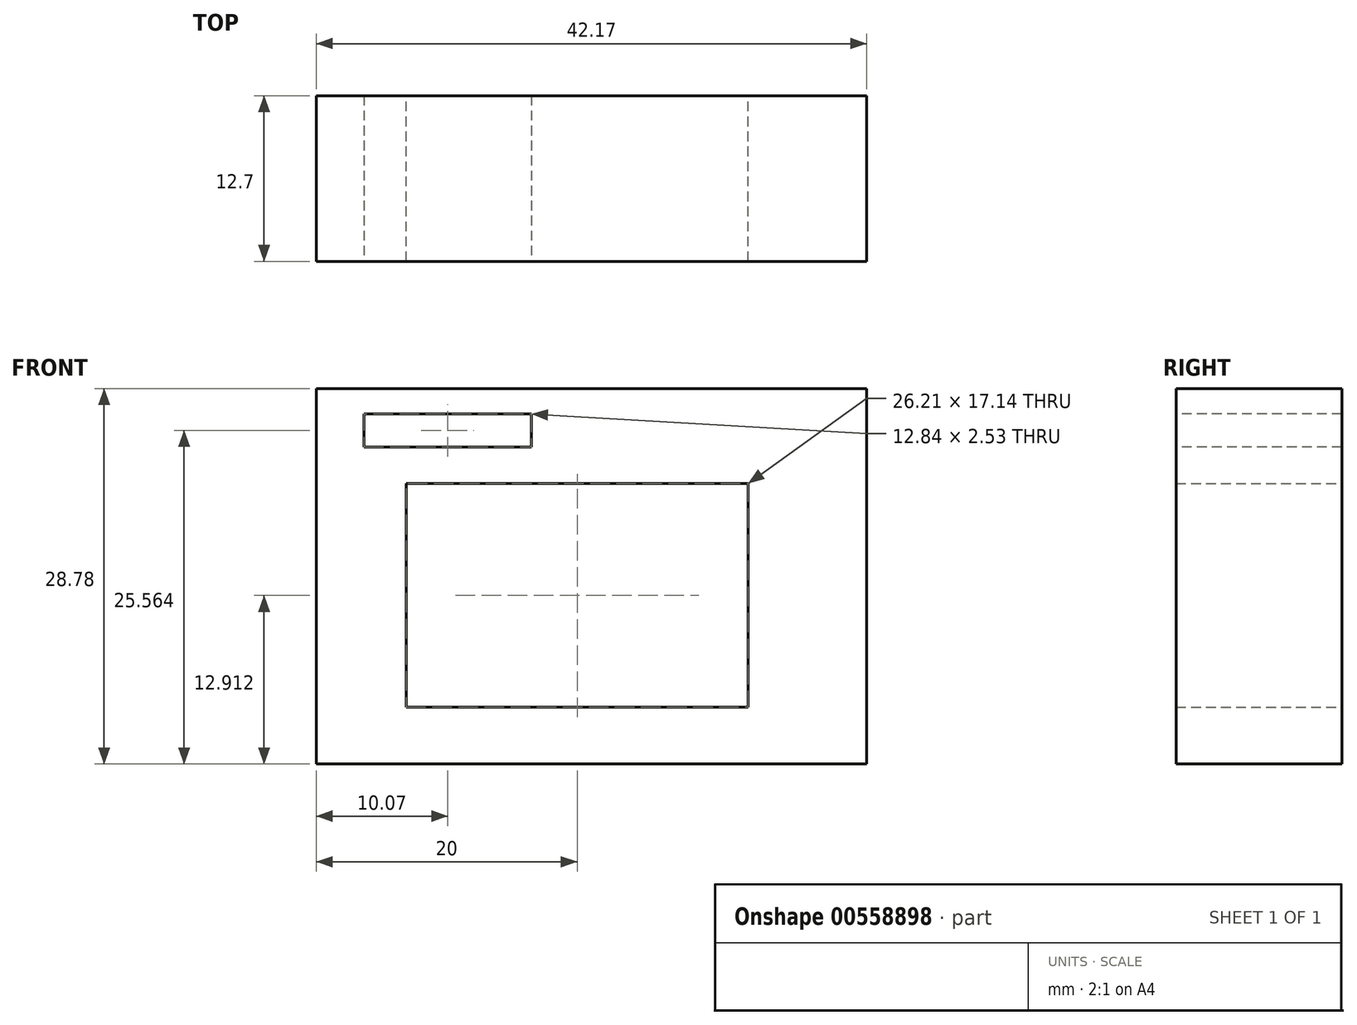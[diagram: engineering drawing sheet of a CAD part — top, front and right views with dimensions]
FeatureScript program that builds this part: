
annotation { "Feature Type Name" : "Feature", "Feature Type Description" : "" }
export const myFeature = defineFeature(function(context is Context, id is Id, definition is map)
    precondition{}
    {
        {
            var Q0;
            Q0=qCreatedBy(makeId("Front.planeOp"),FACE);
            var sketch = newSketch(context, id + "F0", { "sketchPlane" : qUnion([Q0])});
            skLineSegment(sketch, "E0.bottom", {"start": v(-61.68, 40.6) * mm, "end": v(-19.5, 40.6) * mm});
            skLineSegment(sketch, "E0.top", {"start": v(-61.68, 11.82) * mm, "end": v(-19.5, 11.82) * mm});
            skLineSegment(sketch, "E0.left", {"start": v(-61.68, 40.6) * mm, "end": v(-61.68, 11.82) * mm});
            skLineSegment(sketch, "E0.right", {"start": v(-19.5, 40.6) * mm, "end": v(-19.5, 11.82) * mm});
            skLineSegment(sketch, "E1.bottom", {"start": v(-54.79, 33.3) * mm, "end": v(-28.57, 33.3) * mm});
            skLineSegment(sketch, "E1.top", {"start": v(-54.79, 16.16) * mm, "end": v(-28.57, 16.16) * mm});
            skLineSegment(sketch, "E1.left", {"start": v(-54.79, 33.3) * mm, "end": v(-54.79, 16.16) * mm});
            skLineSegment(sketch, "E1.right", {"start": v(-28.57, 33.3) * mm, "end": v(-28.57, 16.16) * mm});
            skSolve(sketch);
        }
        {
            var Q0;
            Q0 = qSketchRegion(id + "F0", true);
            extrude(context, id + "F1", {"entities" : qUnion([Q0]), "depth" : 12.7 * mm, "offsetDistance" : 25.4 * mm});
        }
        {
            var Q0;
            Q0=makeQuery(id+"F1.opExtrude","CAP_FACE",FACE,{"disambiguationData":[OSD([sQuery(id+"F0.wireOp",EDGE,"E0.bottom"),sQuery(id+"F0.wireOp",EDGE,"E0.top"),sQuery(id+"F0.wireOp",EDGE,"E0.left"),sQuery(id+"F0.wireOp",EDGE,"E0.right"),sQuery(id+"F0.wireOp",EDGE,"E1.bottom"),sQuery(id+"F0.wireOp",EDGE,"E1.top"),sQuery(id+"F0.wireOp",EDGE,"E1.left"),sQuery(id+"F0.wireOp",EDGE,"E1.right")])],"isStart":false});
            var sketch = newSketch(context, id + "F2", { "sketchPlane" : qUnion([Q0])});
            skLineSegment(sketch, "E2.bottom", {"start": v(-58.03, 38.65) * mm, "end": v(-45.19, 38.65) * mm});
            skLineSegment(sketch, "E2.top", {"start": v(-58.03, 36.12) * mm, "end": v(-45.19, 36.12) * mm});
            skLineSegment(sketch, "E2.left", {"start": v(-58.03, 38.65) * mm, "end": v(-58.03, 36.12) * mm});
            skLineSegment(sketch, "E2.right", {"start": v(-45.19, 38.65) * mm, "end": v(-45.19, 36.12) * mm});
            skSolve(sketch);
        }
        {
            var Q0;
            Q0 = qSketchRegion(id + "F2", true);
            extrude(context, id + "F3", {"entities" : qUnion([Q0]), "operationType" : NewBodyOperationType.REMOVE, "oppositeDirection" : true, "depth" : 25.4 * mm, "offsetDistance" : 25.4 * mm});
        }
    });
